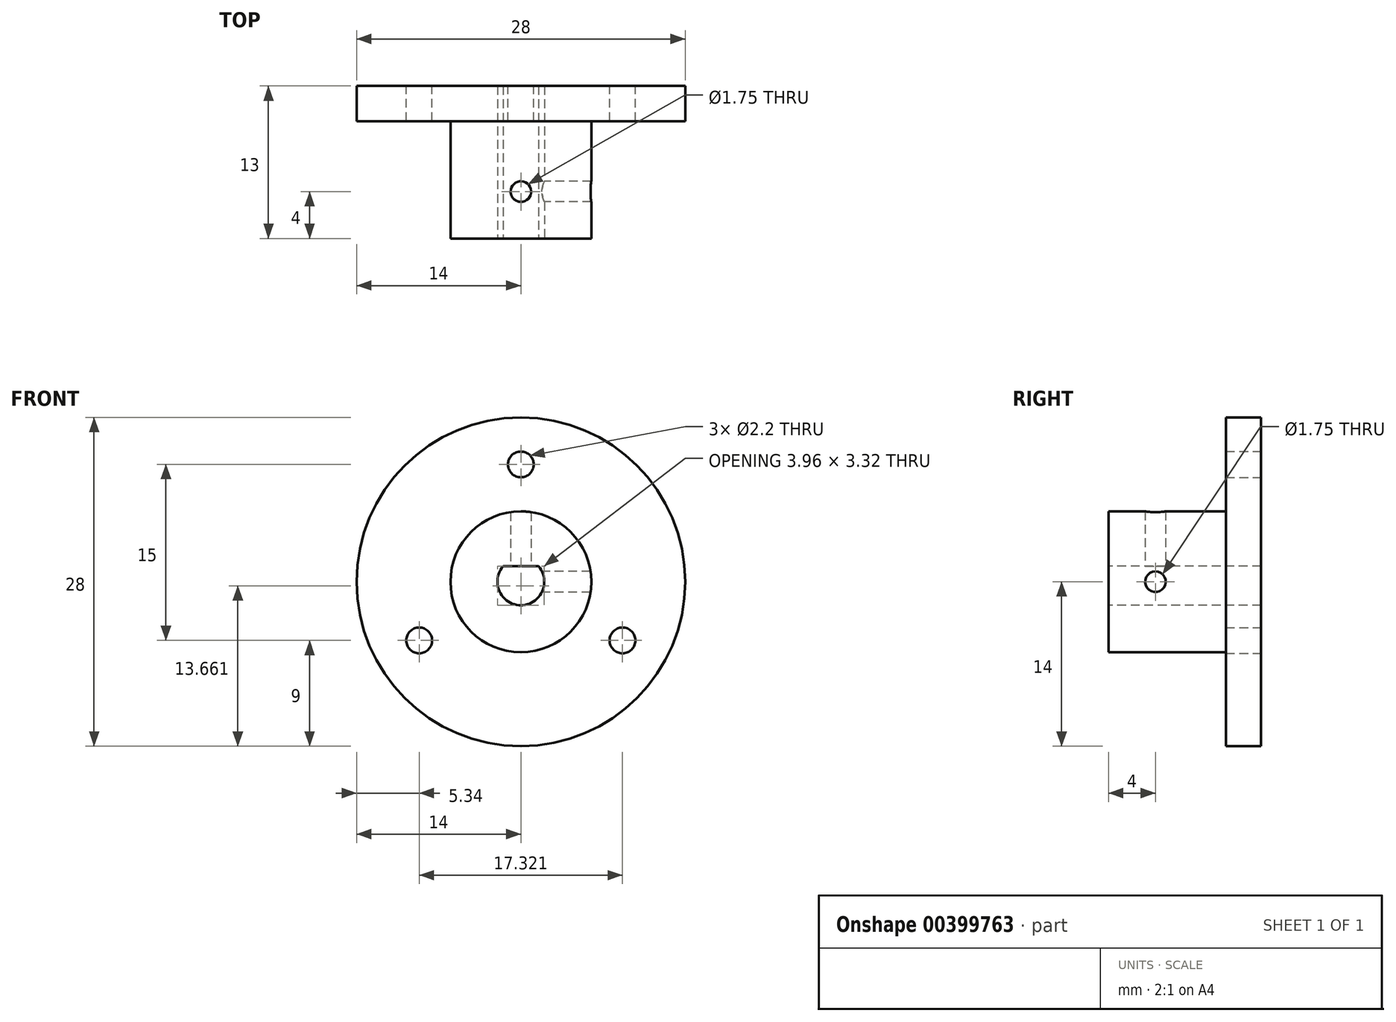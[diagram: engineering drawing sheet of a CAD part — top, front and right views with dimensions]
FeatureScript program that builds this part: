
annotation { "Feature Type Name" : "Feature", "Feature Type Description" : "" }
export const myFeature = defineFeature(function(context is Context, id is Id, definition is map)
    precondition{}
    {
        {
            var Q0;
            Q0=qCreatedBy(makeId("Front.planeOp"),FACE);
            var sketch = newSketch(context, id + "F0", { "sketchPlane" : qUnion([Q0])});
            skCircle(sketch, "E0", {"center": v(0, 0) * mm, "radius": 10 * mm, "construction": true});
            skLineSegment(sketch, "E1.0", {"start": v(0, 10) * mm, "end": v(8.66, -5) * mm, "construction": true});
            skLineSegment(sketch, "E1.1", {"start": v(8.66, -5) * mm, "end": v(-8.66, -5) * mm, "construction": true});
            skLineSegment(sketch, "E1.2", {"start": v(-8.66, -5) * mm, "end": v(0, 10) * mm, "construction": true});
            skCircle(sketch, "E2", {"center": v(0, 10) * mm, "radius": 1.1 * mm});
            skCircle(sketch, "E3", {"center": v(8.66, -5) * mm, "radius": 1.1 * mm});
            skCircle(sketch, "E4", {"center": v(-8.66, -5) * mm, "radius": 1.1 * mm});
            skCircle(sketch, "E5", {"center": v(0, 0) * mm, "radius": 14 * mm});
            skSolve(sketch);
        }
        {
            var Q0;
            Q0=makeQuery(id+"F0.imprint","IMPRINT",FACE,{"disambiguationData":[TD([[makeQuery(id+"F0.imprint","IMPRINT",EDGE,{"derivedFrom":sQuery(id+"F0.wireOp",EDGE,"E2")}),-1.0]])]});
            extrude(context, id + "F1", {"entities" : qUnion([Q0]), "depth" : 3 * mm});
        }
        {
            var Q0;
            Q0=makeQuery(id+"F1.opExtrude","CAP_FACE",FACE,{"disambiguationData":[OSD([sQuery(id+"F0.wireOp",EDGE,"E2"),sQuery(id+"F0.wireOp",EDGE,"E3"),sQuery(id+"F0.wireOp",EDGE,"E4"),sQuery(id+"F0.wireOp",EDGE,"E5")])],"isStart":false});
            var sketch = newSketch(context, id + "F2", { "sketchPlane" : qUnion([Q0])});
            skCircle(sketch, "E6", {"center": v(0, 0) * mm, "radius": 6 * mm});
            skSolve(sketch);
        }
        {
            var Q0;
            Q0 = qSketchRegion(id + "F2", true);
            extrude(context, id + "F3", {"entities" : qUnion([Q0]), "operationType" : NewBodyOperationType.ADD, "depth" : 10 * mm});
        }
        {
            var Q0;
            Q0=makeQuery(id+"F3.opExtrude","CAP_FACE",FACE,{"disambiguationData":[OSD([sQuery(id+"F2.wireOp",EDGE,"E6")])],"isStart":false});
            var sketch = newSketch(context, id + "F4", { "sketchPlane" : qUnion([Q0])});
            skArc(sketch, "E7", {"start": v(-1.5, 1.32) * mm, "mid": v(0, -2) * mm, "end": v(1.5, 1.32) * mm});
            skLineSegment(sketch, "E8.bottom", {"start": v(-1.5, 1.32) * mm, "end": v(1.5, 1.32) * mm});
            skPoint(sketch, "E8.top.start.orphan", {"position": v(-1.5, -1.32) * mm});
            skPoint(sketch, "E8.right.end.orphan", {"position": v(1.5, -1.32) * mm});
            skSolve(sketch);
        }
        {
            var Q0;
            Q0 = qSketchRegion(id + "F4", true);
            extrude(context, id + "F5", {"entities" : qUnion([Q0]), "operationType" : NewBodyOperationType.REMOVE, "endBound" : BoundingType.THROUGH_ALL, "oppositeDirection" : true, "depth" : 25 * mm});
        }
        {
            var Q0;
            Q0=qCreatedBy(makeId("Top.planeOp"),FACE);
            var sketch = newSketch(context, id + "F6", { "sketchPlane" : qUnion([Q0])});
            skCircle(sketch, "E9", {"center": v(0, -9) * mm, "radius": 0.88 * mm});
            skSolve(sketch);
        }
        {
            var Q0;
            Q0 = qSketchRegion(id + "F6", true);
            extrude(context, id + "F7", {"entities" : qUnion([Q0]), "operationType" : NewBodyOperationType.REMOVE, "endBound" : BoundingType.THROUGH_ALL, "depth" : 25 * mm});
        }
        {
            var Q0;
            Q0=qCreatedBy(makeId("Right.planeOp"),FACE);
            var sketch = newSketch(context, id + "F8", { "sketchPlane" : qUnion([Q0])});
            skCircle(sketch, "E10", {"center": v(-9, 0) * mm, "radius": 0.87 * mm});
            skSolve(sketch);
        }
        {
            var Q0;
            Q0 = qSketchRegion(id + "F8", true);
            extrude(context, id + "F9", {"entities" : qUnion([Q0]), "operationType" : NewBodyOperationType.REMOVE, "endBound" : BoundingType.THROUGH_ALL, "depth" : 25 * mm});
        }
    });
